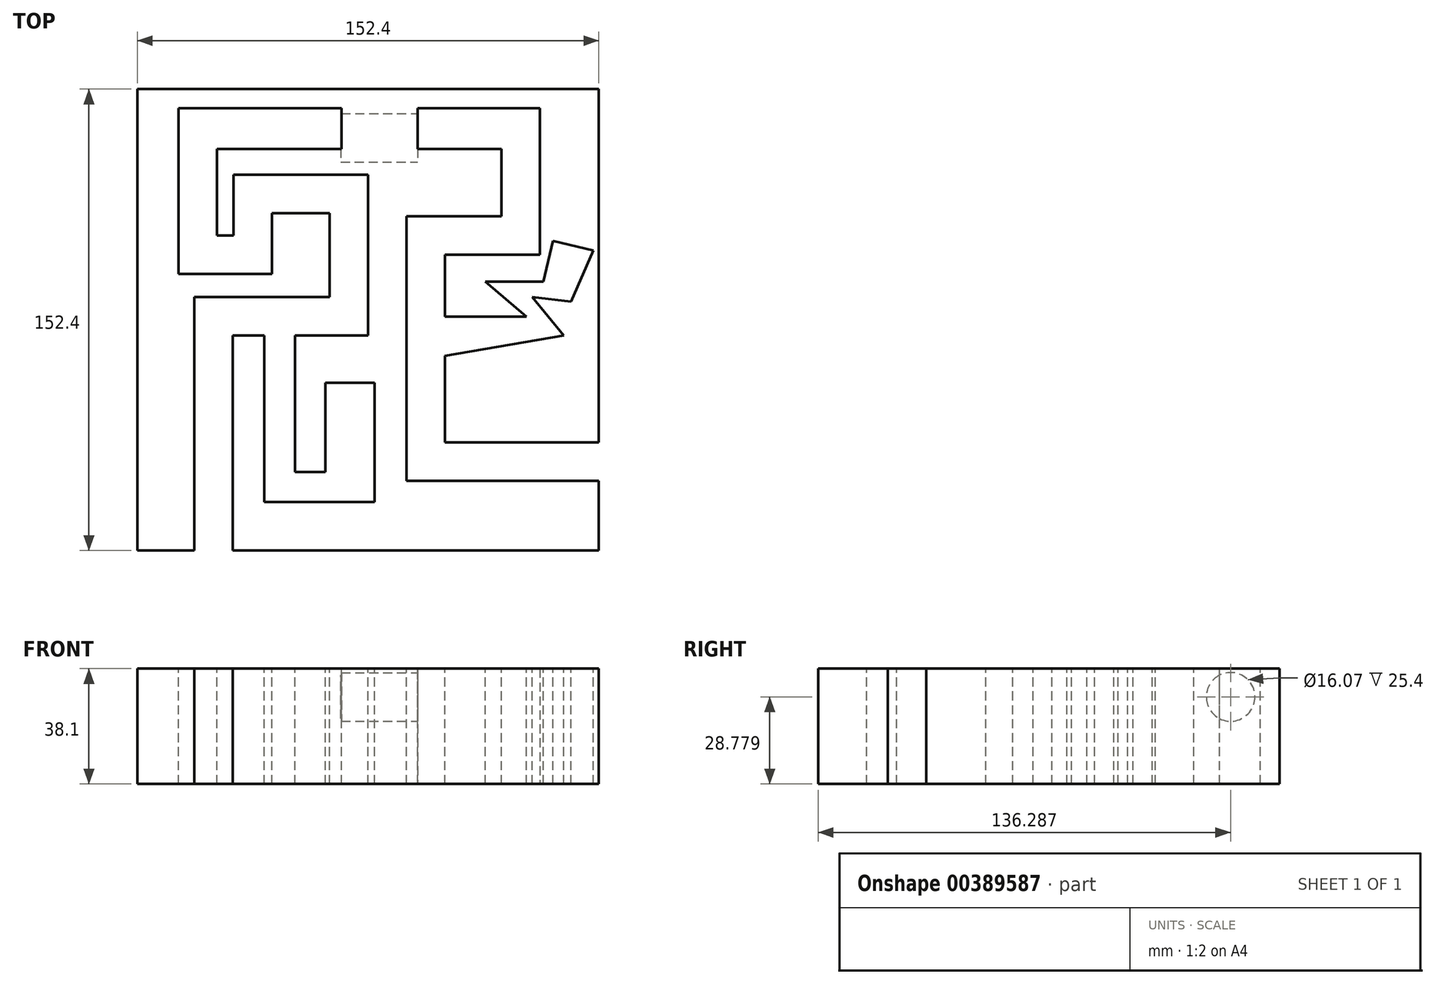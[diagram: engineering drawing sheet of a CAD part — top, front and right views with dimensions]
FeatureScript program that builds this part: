
annotation { "Feature Type Name" : "Feature", "Feature Type Description" : "" }
export const myFeature = defineFeature(function(context is Context, id is Id, definition is map)
    precondition{}
    {
        {
            var Q0;
            Q0=qCreatedBy(makeId("Top.planeOp"),FACE);
            var sketch = newSketch(context, id + "F0", { "sketchPlane" : qUnion([Q0])});
            skLineSegment(sketch, "E0.bottom", {"start": v(-76.2, 68.72) * mm, "end": v(76.2, 68.72) * mm});
            skLineSegment(sketch, "E0.top", {"start": v(-76.2, -83.68) * mm, "end": v(76.2, -83.68) * mm});
            skLineSegment(sketch, "E0.left", {"start": v(-76.2, 68.72) * mm, "end": v(-76.2, -83.68) * mm});
            skLineSegment(sketch, "E0.right", {"start": v(76.2, 68.72) * mm, "end": v(76.2, -83.68) * mm});
            skLineSegment(sketch, "E1.0", {"start": v(-69.85, 62.37) * mm, "end": v(-69.85, -77.33) * mm});
            skLineSegment(sketch, "E1.1", {"start": v(-69.85, 62.37) * mm, "end": v(69.85, 62.37) * mm});
            skLineSegment(sketch, "E1.2", {"start": v(69.85, 62.37) * mm, "end": v(69.85, -77.33) * mm});
            skLineSegment(sketch, "E1.3", {"start": v(-69.85, -77.33) * mm, "end": v(69.85, -77.33) * mm});
            skSolve(sketch);
        }
        {
            var Q0;
            Q0=makeQuery(id+"F0.imprint","IMPRINT",FACE,{"disambiguationData":[TD([[makeQuery(id+"F0.imprint","IMPRINT",EDGE,{"derivedFrom":sQuery(id+"F0.wireOp",EDGE,"E0.bottom")}),-1.0]])]});
            extrude(context, id + "F1", {"entities" : qUnion([Q0]), "depth" : 38.1 * mm});
        }
        {
            var Q0;
            Q0=makeQuery(id+"F1.opExtrude","SWEPT_FACE",FACE,{"disambiguationData":[OSD([sQuery(id+"F0.wireOp",EDGE,"E0.top")])]});
            var sketch = newSketch(context, id + "F2", { "sketchPlane" : qUnion([Q0])});
            skLineSegment(sketch, "E2.bottom", {"start": v(-57.4, 38.1) * mm, "end": v(-44.7, 38.1) * mm});
            skLineSegment(sketch, "E2.top", {"start": v(-57.4, 0) * mm, "end": v(-44.7, 0) * mm});
            skLineSegment(sketch, "E2.left", {"start": v(-57.4, 38.1) * mm, "end": v(-57.4, 0) * mm});
            skLineSegment(sketch, "E2.right", {"start": v(-44.7, 38.1) * mm, "end": v(-44.7, 0) * mm});
            skSolve(sketch);
        }
        {
            var Q0;
            Q0=makeQuery(id+"F2.imprint","IMPRINT",FACE,{"disambiguationData":[TD([[makeQuery(id+"F2.imprint","IMPRINT",EDGE,{"derivedFrom":sQuery(id+"F2.wireOp",EDGE,"E2.bottom")}),-1.0]])]});
            extrude(context, id + "F3", {"entities" : qUnion([Q0]), "operationType" : NewBodyOperationType.REMOVE, "oppositeDirection" : true, "depth" : 37.08 * mm});
        }
        {
            var Q0;
            Q0=makeQuery(id+"F1.opExtrude","CAP_FACE",FACE,{"disambiguationData":[OSD([sQuery(id+"F0.wireOp",EDGE,"E0.bottom"),sQuery(id+"F0.wireOp",EDGE,"E0.top"),sQuery(id+"F0.wireOp",EDGE,"E0.left"),sQuery(id+"F0.wireOp",EDGE,"E0.right"),sQuery(id+"F0.wireOp",EDGE,"E1.0"),sQuery(id+"F0.wireOp",EDGE,"E1.1"),sQuery(id+"F0.wireOp",EDGE,"E1.2"),sQuery(id+"F0.wireOp",EDGE,"E1.3")])],"isStart":false});
            var sketch = newSketch(context, id + "F4", { "sketchPlane" : qUnion([Q0])});
            skLineSegment(sketch, "E3", {"start": v(-57.4, -77.33) * mm, "end": v(-57.4, 0) * mm});
            skLineSegment(sketch, "E4", {"start": v(-57.4, 0) * mm, "end": v(-12.7, 0) * mm});
            skLineSegment(sketch, "E5", {"start": v(-12.7, 0) * mm, "end": v(-12.7, 27.8) * mm});
            skLineSegment(sketch, "E6", {"start": v(-12.7, 27.8) * mm, "end": v(-31.73, 27.8) * mm});
            skLineSegment(sketch, "E7", {"start": v(-31.73, 27.8) * mm, "end": v(-31.73, 7.62) * mm});
            skLineSegment(sketch, "E8", {"start": v(-31.73, 7.62) * mm, "end": v(-62.66, 7.62) * mm});
            skLineSegment(sketch, "E9", {"start": v(-62.66, 7.62) * mm, "end": v(-62.66, 61.67) * mm});
            skLineSegment(sketch, "E10", {"start": v(56.8, 61.68) * mm, "end": v(56.8, 13.98) * mm});
            skLineSegment(sketch, "E11", {"start": v(56.8, 13.98) * mm, "end": v(25.4, 13.98) * mm});
            skLineSegment(sketch, "E12", {"start": v(25.4, 13.98) * mm, "end": v(25.4, -47.97) * mm});
            skLineSegment(sketch, "E13", {"start": v(25.4, -47.97) * mm, "end": v(69.85, -47.97) * mm});
            skLineSegment(sketch, "E14", {"start": v(-44.7, -77.33) * mm, "end": v(-44.7, -12.7) * mm});
            skLineSegment(sketch, "E15", {"start": v(-44.7, -12.7) * mm, "end": v(-34.27, -12.7) * mm});
            skLineSegment(sketch, "E16", {"start": v(0, -12.7) * mm, "end": v(0, 40.5) * mm});
            skLineSegment(sketch, "E17", {"start": v(0, 40.5) * mm, "end": v(-44.43, 40.5) * mm});
            skLineSegment(sketch, "E18", {"start": v(-44.43, 40.5) * mm, "end": v(-44.43, 20.32) * mm});
            skLineSegment(sketch, "E19", {"start": v(-44.43, 20.32) * mm, "end": v(-49.96, 20.32) * mm});
            skLineSegment(sketch, "E20", {"start": v(-49.96, 20.32) * mm, "end": v(-49.96, 48.98) * mm});
            skLineSegment(sketch, "E21", {"start": v(-49.96, 48.98) * mm, "end": v(44.1, 48.98) * mm});
            skLineSegment(sketch, "E22", {"start": v(44.1, 48.98) * mm, "end": v(44.1, 26.68) * mm});
            skLineSegment(sketch, "E23", {"start": v(44.1, 26.68) * mm, "end": v(12.7, 26.68) * mm});
            skLineSegment(sketch, "E24", {"start": v(12.7, 26.68) * mm, "end": v(12.7, -60.67) * mm});
            skLineSegment(sketch, "E25", {"start": v(12.7, -60.67) * mm, "end": v(69.85, -60.67) * mm});
            skLineSegment(sketch, "E26", {"start": v(69.85, -25.59) * mm, "end": v(69.85, -25.59) * mm});
            skLineSegment(sketch, "E27", {"start": v(56.8, 61.68) * mm, "end": v(56.8, 64.87) * mm});
            skLineSegment(sketch, "E28", {"start": v(56.8, 64.87) * mm, "end": v(-62.66, 64.87) * mm});
            skLineSegment(sketch, "E29", {"start": v(-62.66, 64.87) * mm, "end": v(-62.66, 61.67) * mm});
            skLineSegment(sketch, "E30", {"start": v(69.85, -47.97) * mm, "end": v(69.85, 62.37) * mm});
            skLineSegment(sketch, "E31", {"start": v(69.85, 62.37) * mm, "end": v(56.8, 64.87) * mm});
            skLineSegment(sketch, "E32", {"start": v(-34.27, -12.7) * mm, "end": v(-34.27, -67.66) * mm});
            skLineSegment(sketch, "E33", {"start": v(-34.27, -67.66) * mm, "end": v(2.18, -67.66) * mm});
            skLineSegment(sketch, "E34", {"start": v(2.18, -67.66) * mm, "end": v(2.18, -28.22) * mm});
            skLineSegment(sketch, "E35", {"start": v(2.18, -28.22) * mm, "end": v(-14.1, -28.22) * mm});
            skLineSegment(sketch, "E36", {"start": v(-14.1, -28.22) * mm, "end": v(-14.1, -57.8) * mm});
            skLineSegment(sketch, "E37", {"start": v(-14.1, -57.8) * mm, "end": v(-24.19, -57.8) * mm});
            skLineSegment(sketch, "E38", {"start": v(-24.19, -57.8) * mm, "end": v(-24.19, -12.7) * mm});
            skLineSegment(sketch, "E39.trimOffspring", {"start": v(-24.19, -12.7) * mm, "end": v(0, -12.7) * mm});
            skSolve(sketch);
        }
        {
            var Q0;
            Q0 = qSketchRegion(id + "F4", true);
            var Q1;
            Q1=makeQuery(id+"F4.imprint","IMPRINT",FACE,{"disambiguationData":[TD([[makeQuery(id+"F4.imprint","IMPRINT",EDGE,{"derivedFrom":sQuery(id+"F4.wireOp",EDGE,"E3")}),1.0]])]});
            var Q2;
            Q2=makeQuery(id+"F4.imprint","IMPRINT",FACE,{"disambiguationData":[TD([[makeQuery(id+"F4.imprint","IMPRINT",EDGE,{"derivedFrom":sQuery(id+"F4.wireOp",EDGE,"E14")}),-1.0]])]});
            var Q3;
            Q3=makeQuery(id+"F1.opExtrude","CAP_FACE",FACE,{"disambiguationData":[OSD([sQuery(id+"F0.wireOp",EDGE,"E0.bottom"),sQuery(id+"F0.wireOp",EDGE,"E0.top"),sQuery(id+"F0.wireOp",EDGE,"E0.left"),sQuery(id+"F0.wireOp",EDGE,"E0.right"),sQuery(id+"F0.wireOp",EDGE,"E1.0"),sQuery(id+"F0.wireOp",EDGE,"E1.1"),sQuery(id+"F0.wireOp",EDGE,"E1.2"),sQuery(id+"F0.wireOp",EDGE,"E1.3")])],"isStart":true});
            extrude(context, id + "F5", {"entities" : qUnion([Q0, Q1, Q2]), "operationType" : NewBodyOperationType.ADD, "endBound" : BoundingType.UP_TO_SURFACE, "oppositeDirection" : true, "depth" : 25.4 * mm, "endBoundEntityFace" : qUnion([Q3]), "offsetDistance" : 25.4 * mm});
        }
        {
            var Q0;
            {var subQ0=sQuery(id+"F0.wireOp",EDGE,"E1.3");var subQ1=sQuery(id+"F0.wireOp",EDGE,"E1.2");var subQ2=sQuery(id+"F0.wireOp",EDGE,"E1.1");var subQ3=sQuery(id+"F0.wireOp",EDGE,"E1.0");Q0=makeQuery(id+"F5.boolean.opBoolean","MERGE",FACE,{"derivedFrom":[makeQuery(id+"F1.opExtrude","CAP_FACE",FACE,{"disambiguationData":[OSD([sQuery(id+"F0.wireOp",EDGE,"E0.bottom"),sQuery(id+"F0.wireOp",EDGE,"E0.top"),sQuery(id+"F0.wireOp",EDGE,"E0.left"),sQuery(id+"F0.wireOp",EDGE,"E0.right"),subQ3,subQ2,subQ1,subQ0])],"isStart":false}),makeQuery(id+"F5.opExtrude","CAP_FACE",FACE,{"disambiguationData":[OSD([subQ3,subQ2,subQ1,subQ0,sQuery(id+"F4.wireOp",EDGE,"E3"),sQuery(id+"F4.wireOp",EDGE,"E4"),sQuery(id+"F4.wireOp",EDGE,"E5"),sQuery(id+"F4.wireOp",EDGE,"E6"),sQuery(id+"F4.wireOp",EDGE,"E7"),sQuery(id+"F4.wireOp",EDGE,"E8"),sQuery(id+"F4.wireOp",EDGE,"E9"),sQuery(id+"F4.wireOp",EDGE,"8O32yOs5-ra33-InHz-12bj-kFNQWWaEYEYm"),sQuery(id+"F4.wireOp",EDGE,"E10"),sQuery(id+"F4.wireOp",EDGE,"E11"),sQuery(id+"F4.wireOp",EDGE,"E12"),sQuery(id+"F4.wireOp",EDGE,"E13")])],"isStart":true}),makeQuery(id+"F5.opExtrude","CAP_FACE",FACE,{"disambiguationData":[OSD([subQ1,subQ0,sQuery(id+"F4.wireOp",EDGE,"E14"),sQuery(id+"F4.wireOp",EDGE,"E15"),sQuery(id+"F4.wireOp",EDGE,"E16"),sQuery(id+"F4.wireOp",EDGE,"E17"),sQuery(id+"F4.wireOp",EDGE,"E18"),sQuery(id+"F4.wireOp",EDGE,"E19"),sQuery(id+"F4.wireOp",EDGE,"E20"),sQuery(id+"F4.wireOp",EDGE,"E21"),sQuery(id+"F4.wireOp",EDGE,"E22"),sQuery(id+"F4.wireOp",EDGE,"E23"),sQuery(id+"F4.wireOp",EDGE,"E24"),sQuery(id+"F4.wireOp",EDGE,"E25")])],"isStart":true})]});}
            var sketch = newSketch(context, id + "F6", { "sketchPlane" : qUnion([Q0])});
            skLineSegment(sketch, "E40", {"start": v(69.85, -47.97) * mm, "end": v(76.2, -47.97) * mm});
            skLineSegment(sketch, "E41", {"start": v(76.2, -47.97) * mm, "end": v(76.2, -60.67) * mm});
            skLineSegment(sketch, "E42", {"start": v(76.2, -60.67) * mm, "end": v(69.85, -60.67) * mm});
            skLineSegment(sketch, "E43", {"start": v(69.85, -60.67) * mm, "end": v(69.85, -47.97) * mm});
            skSolve(sketch);
        }
        {
            var Q0;
            Q0 = qSketchRegion(id + "F6", true);
            extrude(context, id + "F7", {"entities" : qUnion([Q0]), "operationType" : NewBodyOperationType.REMOVE, "endBound" : BoundingType.THROUGH_ALL, "oppositeDirection" : true, "depth" : 25.4 * mm, "offsetDistance" : 25.4 * mm});
        }
        {
            var Q0;
            {var subQ0=sQuery(id+"F4.wireOp",EDGE,"E5");var subQ1=sQuery(id+"F4.wireOp",EDGE,"E4");var subQ2=sQuery(id+"F0.wireOp",EDGE,"E0.right");var subQ3=sQuery(id+"F4.wireOp",EDGE,"E3");var subQ4=sQuery(id+"F0.wireOp",EDGE,"E0.top");var subQ5=sQuery(id+"F0.wireOp",EDGE,"E1.1");var subQ6=sQuery(id+"F4.wireOp",EDGE,"E6");var subQ7=sQuery(id+"F0.wireOp",EDGE,"E0.bottom");var subQ8=sQuery(id+"F4.wireOp",EDGE,"E11");var subQ9=sQuery(id+"F0.wireOp",EDGE,"E0.left");var subQ10=sQuery(id+"F4.wireOp",EDGE,"E7");var subQ11=sQuery(id+"F4.wireOp",EDGE,"E8");var subQ12=sQuery(id+"F4.wireOp",EDGE,"E29");var subQ13=sQuery(id+"F4.wireOp",EDGE,"E9");var subQ14=sQuery(id+"F4.wireOp",EDGE,"E27");var subQ15=sQuery(id+"F4.wireOp",EDGE,"E10");var subQ16=sQuery(id+"F4.wireOp",EDGE,"E12");var subQ17=sQuery(id+"F4.wireOp",EDGE,"E13");var subQ18=sQuery(id+"F0.wireOp",EDGE,"E1.3");var subQ19=sQuery(id+"F0.wireOp",EDGE,"E1.2");var subQ20=sQuery(id+"F0.wireOp",EDGE,"E1.0");Q0=makeQuery(id+"F7.boolean.opBoolean","SPLIT",FACE,{"disambiguationData":[TD([makeQuery(id+"F1.opExtrude","SWEPT_FACE",FACE,{"disambiguationData":[OSD([subQ7])]})])],"derivedFrom":makeQuery(id+"F5.boolean.opBoolean","MERGE",FACE,{"derivedFrom":[makeQuery(id+"F1.opExtrude","CAP_FACE",FACE,{"disambiguationData":[OSD([subQ7,subQ4,subQ9,subQ2,subQ20,subQ5,subQ19,subQ18])],"isStart":false}),makeQuery(id+"F5.opExtrude","CAP_FACE",FACE,{"disambiguationData":[OSD([subQ20,subQ5,subQ18,subQ3,subQ1,subQ0,subQ6,subQ10,subQ11,subQ13,subQ12])],"isStart":true}),makeQuery(id+"F5.opExtrude","CAP_FACE",FACE,{"disambiguationData":[OSD([subQ15,subQ8,subQ16,subQ17,subQ14,sQuery(id+"F4.wireOp",EDGE,"E30"),sQuery(id+"F4.wireOp",EDGE,"E31")])],"isStart":true}),makeQuery(id+"F5.opExtrude","CAP_FACE",FACE,{"disambiguationData":[OSD([subQ19,subQ18,sQuery(id+"F4.wireOp",EDGE,"E14"),sQuery(id+"F4.wireOp",EDGE,"E15"),sQuery(id+"F4.wireOp",EDGE,"E16"),sQuery(id+"F4.wireOp",EDGE,"E17"),sQuery(id+"F4.wireOp",EDGE,"E18"),sQuery(id+"F4.wireOp",EDGE,"E19"),sQuery(id+"F4.wireOp",EDGE,"E20"),sQuery(id+"F4.wireOp",EDGE,"E21"),sQuery(id+"F4.wireOp",EDGE,"E22"),sQuery(id+"F4.wireOp",EDGE,"E23"),sQuery(id+"F4.wireOp",EDGE,"E24"),sQuery(id+"F4.wireOp",EDGE,"E25"),sQuery(id+"F4.wireOp",EDGE,"E32"),sQuery(id+"F4.wireOp",EDGE,"E33"),sQuery(id+"F4.wireOp",EDGE,"E34"),sQuery(id+"F4.wireOp",EDGE,"E35"),sQuery(id+"F4.wireOp",EDGE,"E36"),sQuery(id+"F4.wireOp",EDGE,"E37"),sQuery(id+"F4.wireOp",EDGE,"E38"),sQuery(id+"F4.wireOp",EDGE,"E39.trimOffspring")])],"isStart":true})]})});}
            var sketch = newSketch(context, id + "F8", { "sketchPlane" : qUnion([Q0])});
            skLineSegment(sketch, "E44", {"start": v(25.4, -6.46) * mm, "end": v(52.28, -6.46) * mm});
            skLineSegment(sketch, "E45", {"start": v(52.28, -6.46) * mm, "end": v(38.78, 5.1) * mm});
            skLineSegment(sketch, "E46", {"start": v(38.78, 5.1) * mm, "end": v(57.87, 5.1) * mm});
            skLineSegment(sketch, "E47", {"start": v(57.87, 5.1) * mm, "end": v(61.15, 18.6) * mm});
            skLineSegment(sketch, "E48", {"start": v(61.15, 18.6) * mm, "end": v(74.45, 15.36) * mm});
            skLineSegment(sketch, "E49", {"start": v(74.45, 15.36) * mm, "end": v(67.12, -1.45) * mm});
            skLineSegment(sketch, "E50", {"start": v(67.12, -1.45) * mm, "end": v(54.2, 0) * mm});
            skLineSegment(sketch, "E51", {"start": v(54.2, 0) * mm, "end": v(64.62, -12.63) * mm});
            skLineSegment(sketch, "E52", {"start": v(64.62, -12.63) * mm, "end": v(25.4, -19.38) * mm});
            skLineSegment(sketch, "E53", {"start": v(25.4, -19.38) * mm, "end": v(25.4, -6.46) * mm});
            skSolve(sketch);
        }
        {
            var Q0;
            Q0 = qSketchRegion(id + "F8", true);
            extrude(context, id + "F9", {"entities" : qUnion([Q0]), "operationType" : NewBodyOperationType.REMOVE, "endBound" : BoundingType.THROUGH_ALL, "oppositeDirection" : true, "depth" : 25.4 * mm, "offsetDistance" : 25.4 * mm});
        }
        {
            var Q0;
            {var subQ0=sQuery(id+"F4.wireOp",EDGE,"E37");var subQ1=sQuery(id+"F4.wireOp",EDGE,"E36");var subQ2=sQuery(id+"F4.wireOp",EDGE,"E35");var subQ3=sQuery(id+"F4.wireOp",EDGE,"E34");var subQ4=sQuery(id+"F4.wireOp",EDGE,"E33");var subQ5=sQuery(id+"F4.wireOp",EDGE,"E32");var subQ6=sQuery(id+"F4.wireOp",EDGE,"E24");var subQ7=sQuery(id+"F4.wireOp",EDGE,"E22");var subQ8=sQuery(id+"F4.wireOp",EDGE,"E21");var subQ9=sQuery(id+"F4.wireOp",EDGE,"E14");var subQ10=sQuery(id+"F4.wireOp",EDGE,"E38");var subQ11=sQuery(id+"F4.wireOp",EDGE,"E18");var subQ12=sQuery(id+"F4.wireOp",EDGE,"E25");var subQ13=sQuery(id+"F0.wireOp",EDGE,"E0.right");var subQ14=sQuery(id+"F4.wireOp",EDGE,"E17");var subQ15=sQuery(id+"F4.wireOp",EDGE,"E23");var subQ16=sQuery(id+"F0.wireOp",EDGE,"E0.top");var subQ17=sQuery(id+"F4.wireOp",EDGE,"E15");var subQ18=sQuery(id+"F4.wireOp",EDGE,"E16");var subQ19=sQuery(id+"F4.wireOp",EDGE,"E19");var subQ20=sQuery(id+"F4.wireOp",EDGE,"E20");var subQ21=sQuery(id+"F4.wireOp",EDGE,"E39.trimOffspring");var subQ22=sQuery(id+"F0.wireOp",EDGE,"E1.3");var subQ23=sQuery(id+"F0.wireOp",EDGE,"E1.2");var subQ24=sQuery(id+"F0.wireOp",EDGE,"E1.1");var subQ25=sQuery(id+"F0.wireOp",EDGE,"E1.0");Q0=makeQuery(id+"F7.boolean.opBoolean","SPLIT",FACE,{"disambiguationData":[TD([makeQuery(id+"F3.boolean.opBoolean","COPY",FACE,{"derivedFrom":makeQuery(id+"F3.opExtrude","SWEPT_FACE",FACE,{"disambiguationData":[OSD([sQuery(id+"F2.wireOp",EDGE,"E2.right")])]})})])],"derivedFrom":makeQuery(id+"F5.boolean.opBoolean","MERGE",FACE,{"derivedFrom":[makeQuery(id+"F1.opExtrude","CAP_FACE",FACE,{"disambiguationData":[OSD([sQuery(id+"F0.wireOp",EDGE,"E0.bottom"),subQ16,sQuery(id+"F0.wireOp",EDGE,"E0.left"),subQ13,subQ25,subQ24,subQ23,subQ22])],"isStart":false}),makeQuery(id+"F5.opExtrude","CAP_FACE",FACE,{"disambiguationData":[OSD([subQ25,subQ24,subQ22,sQuery(id+"F4.wireOp",EDGE,"E3"),sQuery(id+"F4.wireOp",EDGE,"E4"),sQuery(id+"F4.wireOp",EDGE,"E5"),sQuery(id+"F4.wireOp",EDGE,"E6"),sQuery(id+"F4.wireOp",EDGE,"E7"),sQuery(id+"F4.wireOp",EDGE,"E8"),sQuery(id+"F4.wireOp",EDGE,"E9"),sQuery(id+"F4.wireOp",EDGE,"E29")])],"isStart":true}),makeQuery(id+"F5.opExtrude","CAP_FACE",FACE,{"disambiguationData":[OSD([sQuery(id+"F4.wireOp",EDGE,"E10"),sQuery(id+"F4.wireOp",EDGE,"E11"),sQuery(id+"F4.wireOp",EDGE,"E12"),sQuery(id+"F4.wireOp",EDGE,"E13"),sQuery(id+"F4.wireOp",EDGE,"E27"),sQuery(id+"F4.wireOp",EDGE,"E30"),sQuery(id+"F4.wireOp",EDGE,"E31")])],"isStart":true}),makeQuery(id+"F5.opExtrude","CAP_FACE",FACE,{"disambiguationData":[OSD([subQ23,subQ22,subQ9,subQ17,subQ18,subQ14,subQ11,subQ19,subQ20,subQ8,subQ7,subQ15,subQ6,subQ12,subQ5,subQ4,subQ3,subQ2,subQ1,subQ0,subQ10,subQ21])],"isStart":true})]})});}
            var sketch = newSketch(context, id + "F10", { "sketchPlane" : qUnion([Q0])});
            skLineSegment(sketch, "E54", {"start": v(-8.83, 62.56) * mm, "end": v(-8.83, 48.98) * mm});
            skLineSegment(sketch, "E55", {"start": v(-8.83, 48.98) * mm, "end": v(16.4, 48.98) * mm});
            skLineSegment(sketch, "E56", {"start": v(16.4, 48.98) * mm, "end": v(16.4, 63.02) * mm});
            skLineSegment(sketch, "E57", {"start": v(16.4, 63.02) * mm, "end": v(-10.89, 62.56) * mm});
            skLineSegment(sketch, "E58", {"start": v(-10.89, 62.56) * mm, "end": v(-8.83, 62.56) * mm});
            skSolve(sketch);
        }
        {
            var Q0;
            Q0 = qSketchRegion(id + "F10", true);
            extrude(context, id + "F11", {"entities" : qUnion([Q0]), "operationType" : NewBodyOperationType.ADD, "oppositeDirection" : true, "depth" : 38.1 * mm, "offsetDistance" : 25.4 * mm});
        }
        {
            var Q0;
            Q0=makeQuery(id+"F11.opExtrude","SWEPT_FACE",FACE,{"disambiguationData":[OSD([sQuery(id+"F10.wireOp",EDGE,"E56")])]});
            var sketch = newSketch(context, id + "F12", { "sketchPlane" : qUnion([Q0])});
            skCircle(sketch, "E59", {"center": v(52.6, 28.78) * mm, "radius": 8.03 * mm});
            skSolve(sketch);
        }
        {
            var Q0;
            Q0 = qSketchRegion(id + "F12", true);
            extrude(context, id + "F13", {"entities" : qUnion([Q0]), "operationType" : NewBodyOperationType.REMOVE, "oppositeDirection" : true, "depth" : 25.4 * mm, "offsetDistance" : 25.4 * mm});
        }
    });
